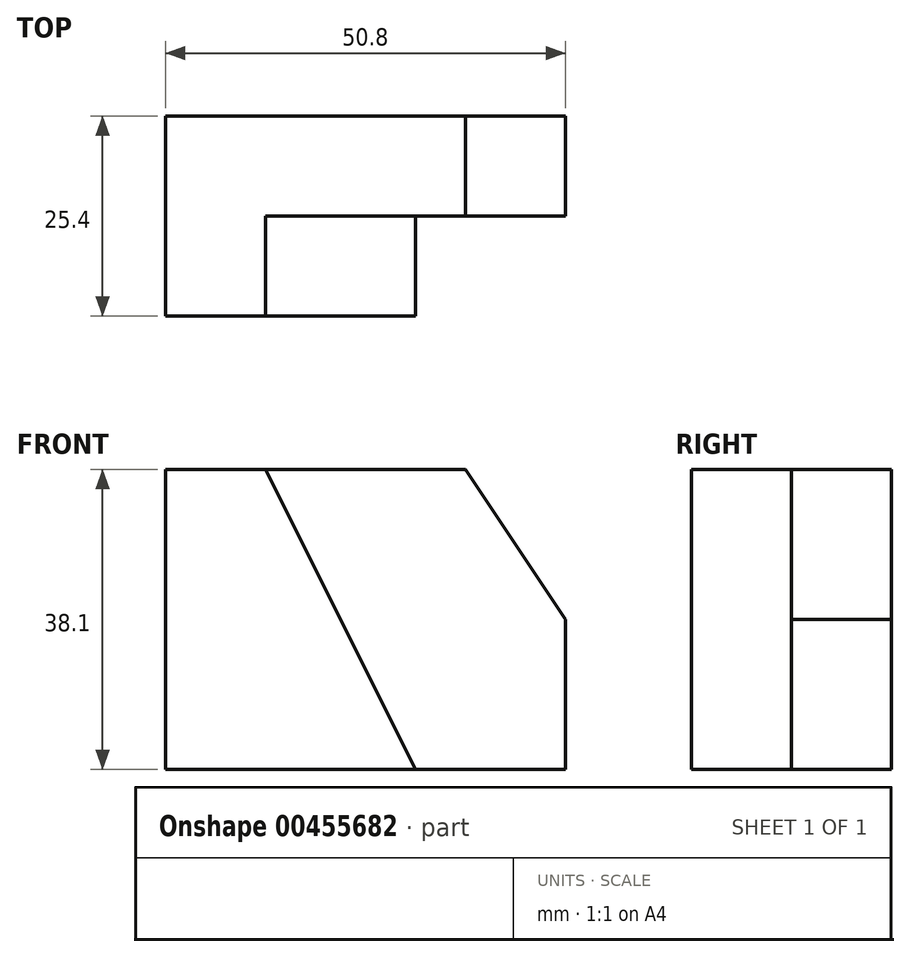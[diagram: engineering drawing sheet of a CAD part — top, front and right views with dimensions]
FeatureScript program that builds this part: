
annotation { "Feature Type Name" : "Feature", "Feature Type Description" : "" }
export const myFeature = defineFeature(function(context is Context, id is Id, definition is map)
    precondition{}
    {
        {
            var Q0;
            Q0=qCreatedBy(makeId("Front.planeOp"),FACE);
            var sketch = newSketch(context, id + "F0", { "sketchPlane" : qUnion([Q0])});
            skLineSegment(sketch, "E0", {"start": v(0, 0) * mm, "end": v(-50.8, 0) * mm});
            skLineSegment(sketch, "E1", {"start": v(-50.8, 0) * mm, "end": v(-50.8, 38.1) * mm});
            skLineSegment(sketch, "E2", {"start": v(-50.8, 38.1) * mm, "end": v(-12.7, 38.1) * mm});
            skLineSegment(sketch, "E3", {"start": v(0, 0) * mm, "end": v(0, 19.05) * mm});
            skPoint(sketch, "E3.endSnap0", {"position": v(-50.8, 19.05) * mm});
            skLineSegment(sketch, "E4", {"start": v(0, 19.05) * mm, "end": v(-12.7, 38.1) * mm});
            skSolve(sketch);
        }
        {
            var Q0;
            Q0 = qSketchRegion(id + "F0", true);
            extrude(context, id + "F1", {"entities" : qUnion([Q0]), "depth" : 12.7 * mm, "offsetDistance" : 25.4 * mm});
        }
        {
            var Q0;
            Q0=makeQuery(id+"F1.opExtrude","CAP_FACE",FACE,{"disambiguationData":[OSD([sQuery(id+"F0.wireOp",EDGE,"E0"),sQuery(id+"F0.wireOp",EDGE,"E1"),sQuery(id+"F0.wireOp",EDGE,"E2"),sQuery(id+"F0.wireOp",EDGE,"E3"),sQuery(id+"F0.wireOp",EDGE,"E4")])],"isStart":false});
            var sketch = newSketch(context, id + "F2", { "sketchPlane" : qUnion([Q0])});
            skLineSegment(sketch, "E5", {"start": v(-50.8, 38.1) * mm, "end": v(-38.1, 38.1) * mm});
            skLineSegment(sketch, "E6", {"start": v(-50.8, 0) * mm, "end": v(-19.05, 0) * mm});
            skLineSegment(sketch, "E7", {"start": v(-19.05, 0) * mm, "end": v(-38.1, 38.1) * mm});
            skLineSegment(sketch, "E8", {"start": v(-50.8, 38.1) * mm, "end": v(-50.8, 0) * mm});
            skSolve(sketch);
        }
        {
            var Q0;
            Q0=makeQuery(id+"F2.imprint","IMPRINT",FACE,{"disambiguationData":[TD([[makeQuery(id+"F2.imprint","IMPRINT",EDGE,{"derivedFrom":sQuery(id+"F2.wireOp",EDGE,"E5")}),-1.0]])]});
            extrude(context, id + "F3", {"entities" : qUnion([Q0]), "operationType" : NewBodyOperationType.ADD, "depth" : 12.7 * mm, "offsetDistance" : 25.4 * mm});
        }
    });
